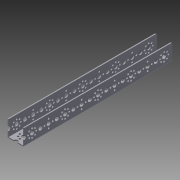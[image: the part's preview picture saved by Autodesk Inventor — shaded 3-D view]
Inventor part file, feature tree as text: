
AUTODESK INVENTOR PART (.ipt)
format: ipt  version: 2014 SP2 (Build 180246200, 246)  size: 729,088 bytes
history: native  units: in
note: dims shown in document units (in); Inventor stores cm internally (conversion verified against a paired STEP export)
features: extrude x2, sketch x2, other x1, imported_body x1
ambient origin geometry x8: Origin, YZ Plane, XZ Plane, XY Plane, X Axis, Y Axis, Z Axis, Center Point
bodies: Solid1 (feature_tree)
feature tree (6):
  other  "416mm Channel.sat1"
  extrude  "Extrusion1"  Depth=4.3307in TaperAngle=0.0deg
  extrude  "Extrusion3"  [1 undecoded]
  imported_body  "Base1"
  sketch  "Sketch2"  dims[d1=3.1208in d2=0.0in d5=4.3307in d6=0.0in]
  sketch  "Sketch4"
note: 1 required parameter value undecoded (feature->parameter linkage not recoverable at this tier; creation-order binding heuristic only, values carry confidence <= 0.55)
